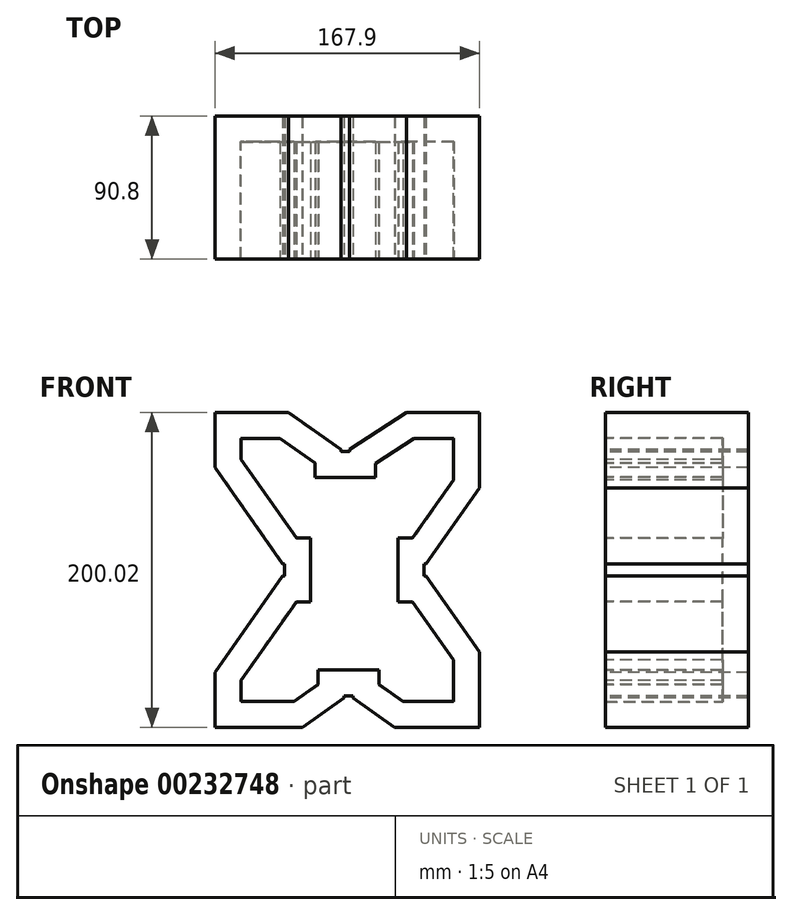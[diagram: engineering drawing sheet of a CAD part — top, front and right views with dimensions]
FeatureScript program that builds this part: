
annotation { "Feature Type Name" : "Feature", "Feature Type Description" : "" }
export const myFeature = defineFeature(function(context is Context, id is Id, definition is map)
    precondition{}
    {
        {
            var Q0;
            Q0=qCreatedBy(makeId("Front.planeOp"),FACE);
            var sketch = newSketch(context, id + "F0", { "sketchPlane" : qUnion([Q0])});
            skLineSegment(sketch, "E0.bottom", {"start": v(83.95, 100.01) * mm, "end": v(-83.95, 100.01) * mm});
            skLineSegment(sketch, "E0.top", {"start": v(83.95, -100.01) * mm, "end": v(-83.95, -100.01) * mm});
            skLineSegment(sketch, "E0.left", {"start": v(83.95, 100.01) * mm, "end": v(83.95, -100.01) * mm});
            skLineSegment(sketch, "E0.right", {"start": v(-83.95, 100.01) * mm, "end": v(-83.95, -100.01) * mm});
            skPoint(sketch, "E0.middle", {"position": v(0, 0) * mm});
            skSolve(sketch);
        }
        {
            var Q0;
            Q0 = qSketchRegion(id + "F0", true);
            extrude(context, id + "F1", {"entities" : qUnion([Q0]), "depth" : 90.8 * mm});
        }
        {
            var Q0;
            Q0=makeQuery(id+"F1.opExtrude","CAP_FACE",FACE,{"disambiguationData":[OSD([sQuery(id+"F0.wireOp",EDGE,"E0.bottom"),sQuery(id+"F0.wireOp",EDGE,"E0.top"),sQuery(id+"F0.wireOp",EDGE,"E0.left"),sQuery(id+"F0.wireOp",EDGE,"E0.right")])],"isStart":false});
            var sketch = newSketch(context, id + "F2", { "sketchPlane" : qUnion([Q0])});
            skLineSegment(sketch, "E1", {"start": v(-83.95, 100.01) * mm, "end": v(-37.47, 100.01) * mm});
            skLineSegment(sketch, "E2", {"start": v(-37.47, 100.01) * mm, "end": v(-3.94, 76.54) * mm});
            skLineSegment(sketch, "E3", {"start": v(-3.94, 76.54) * mm, "end": v(1.52, 76.54) * mm});
            skLineSegment(sketch, "E4", {"start": v(83.95, 100.01) * mm, "end": v(37.46, 100.01) * mm});
            skLineSegment(sketch, "E5", {"start": v(1.52, 76.54) * mm, "end": v(37.47, 100.01) * mm});
            skLineSegment(sketch, "E6", {"start": v(-83.95, 100.01) * mm, "end": v(-83.95, 65.09) * mm});
            skLineSegment(sketch, "E7", {"start": v(-83.95, -100.01) * mm, "end": v(-83.95, -65.09) * mm});
            skLineSegment(sketch, "E8", {"start": v(83.95, -100.01) * mm, "end": v(83.95, -51.98) * mm});
            skLineSegment(sketch, "E9", {"start": v(83.95, -100.01) * mm, "end": v(30.15, -100.01) * mm});
            skLineSegment(sketch, "E10", {"start": v(-83.95, -100.01) * mm, "end": v(-28.58, -100.01) * mm});
            skLineSegment(sketch, "E11", {"start": v(83.95, 100.01) * mm, "end": v(83.95, 51.98) * mm});
            skLineSegment(sketch, "E12", {"start": v(-83.95, 65.09) * mm, "end": v(-40.97, 3.7) * mm});
            skLineSegment(sketch, "E13", {"start": v(-40.97, -3.7) * mm, "end": v(-40.97, 3.7) * mm});
            skLineSegment(sketch, "E14", {"start": v(-83.95, -65.09) * mm, "end": v(-40.97, -3.7) * mm});
            skPoint(sketch, "E15.orphan", {"position": v(-40.97, -13.72) * mm});
            skLineSegment(sketch, "E16", {"start": v(83.95, 51.98) * mm, "end": v(50.15, 3.7) * mm});
            skLineSegment(sketch, "E17", {"start": v(83.95, -51.98) * mm, "end": v(50.15, -3.7) * mm});
            skLineSegment(sketch, "E18", {"start": v(50.15, -3.7) * mm, "end": v(50.15, 3.7) * mm});
            skLineSegment(sketch, "E19", {"start": v(-28.58, -100.01) * mm, "end": v(-1.94, -81.36) * mm});
            skLineSegment(sketch, "E20", {"start": v(-1.94, -81.36) * mm, "end": v(3.52, -81.36) * mm});
            skLineSegment(sketch, "E21", {"start": v(3.52, -81.36) * mm, "end": v(30.15, -100.01) * mm});
            skLineSegment(sketch, "E22", {"start": v(-83.95, 65.09) * mm, "end": v(-83.95, -65.09) * mm});
            skLineSegment(sketch, "E23", {"start": v(-37.47, 100.01) * mm, "end": v(37.46, 100.01) * mm});
            skLineSegment(sketch, "E24", {"start": v(83.95, 51.98) * mm, "end": v(83.95, -51.98) * mm});
            skLineSegment(sketch, "E25", {"start": v(30.15, -100.01) * mm, "end": v(-28.58, -100.01) * mm});
            skLineSegment(sketch, "E26", {"start": v(-3.94, 76.54) * mm, "end": v(-3.94, 75.27) * mm});
            skLineSegment(sketch, "E27", {"start": v(1.52, 75.27) * mm, "end": v(-3.94, 75.27) * mm});
            skLineSegment(sketch, "E28", {"start": v(1.52, 76.54) * mm, "end": v(1.52, 75.27) * mm});
            skLineSegment(sketch, "E29", {"start": v(50.15, 3.7) * mm, "end": v(48.88, 3.7) * mm});
            skLineSegment(sketch, "E30", {"start": v(48.88, -3.7) * mm, "end": v(48.88, 3.7) * mm});
            skLineSegment(sketch, "E31", {"start": v(48.88, -3.7) * mm, "end": v(50.15, -3.7) * mm});
            skLineSegment(sketch, "E32", {"start": v(-40.97, 3.7) * mm, "end": v(-39.7, 3.7) * mm});
            skLineSegment(sketch, "E33", {"start": v(-40.97, -3.7) * mm, "end": v(-39.7, -3.7) * mm});
            skLineSegment(sketch, "E34", {"start": v(-39.7, -3.7) * mm, "end": v(-39.7, 3.7) * mm});
            skLineSegment(sketch, "E35", {"start": v(-1.94, -81.36) * mm, "end": v(-1.94, -80.1) * mm});
            skLineSegment(sketch, "E36", {"start": v(-1.94, -80.1) * mm, "end": v(3.52, -80.1) * mm});
            skLineSegment(sketch, "E37", {"start": v(3.52, -80.1) * mm, "end": v(3.52, -81.36) * mm});
            skSolve(sketch);
        }
        {
            var Q0;
            Q0=makeQuery(id+"F2.imprint","IMPRINT",FACE,{"disambiguationData":[TD([[makeQuery(id+"F2.imprint","IMPRINT",EDGE,{"derivedFrom":sQuery(id+"F2.wireOp",EDGE,"E2")}),1.0]])]});
            var Q1;
            Q1=makeQuery(id+"F2.imprint","IMPRINT",FACE,{"disambiguationData":[TD([[makeQuery(id+"F2.imprint","IMPRINT",EDGE,{"derivedFrom":sQuery(id+"F2.wireOp",EDGE,"E12")}),-1.0]])]});
            var Q2;
            Q2=makeQuery(id+"F2.imprint","IMPRINT",FACE,{"disambiguationData":[TD([[makeQuery(id+"F2.imprint","IMPRINT",EDGE,{"derivedFrom":sQuery(id+"F2.wireOp",EDGE,"E16")}),1.0]])]});
            var Q3;
            Q3=makeQuery(id+"F2.imprint","IMPRINT",FACE,{"disambiguationData":[TD([[makeQuery(id+"F2.imprint","IMPRINT",EDGE,{"derivedFrom":sQuery(id+"F2.wireOp",EDGE,"E19")}),-1.0]])]});
            var Q4;
            Q4=makeQuery(id+"F2.imprint","IMPRINT",FACE,{"disambiguationData":[TD([[makeQuery(id+"F2.imprint","IMPRINT",EDGE,{"derivedFrom":sQuery(id+"F2.wireOp",EDGE,"E13")}),-1.0]])]});
            var Q5;
            Q5=makeQuery(id+"F2.imprint","IMPRINT",FACE,{"disambiguationData":[TD([[makeQuery(id+"F2.imprint","IMPRINT",EDGE,{"derivedFrom":sQuery(id+"F2.wireOp",EDGE,"E18")}),1.0]])]});
            var Q6;
            Q6=makeQuery(id+"F2.imprint","IMPRINT",FACE,{"disambiguationData":[TD([[makeQuery(id+"F2.imprint","IMPRINT",EDGE,{"derivedFrom":sQuery(id+"F2.wireOp",EDGE,"E3")}),-1.0]])]});
            var Q7;
            Q7=makeQuery(id+"F2.imprint","IMPRINT",FACE,{"disambiguationData":[TD([[makeQuery(id+"F2.imprint","IMPRINT",EDGE,{"derivedFrom":sQuery(id+"F2.wireOp",EDGE,"E20")}),1.0]])]});
            extrude(context, id + "F3", {"entities" : qUnion([Q0, Q1, Q2, Q3, Q4, Q5, Q6, Q7]), "operationType" : NewBodyOperationType.REMOVE, "endBound" : BoundingType.THROUGH_ALL, "oppositeDirection" : true, "depth" : 25.4 * mm});
        }
        {
            var Q0;
            Q0=makeQuery(id+"F1.opExtrude","CAP_FACE",FACE,{"disambiguationData":[OSD([sQuery(id+"F0.wireOp",EDGE,"E0.bottom"),sQuery(id+"F0.wireOp",EDGE,"E0.top"),sQuery(id+"F0.wireOp",EDGE,"E0.left"),sQuery(id+"F0.wireOp",EDGE,"E0.right")])],"isStart":false});
            shell(context, id + "F4", {"entities" : qUnion([Q0]), "thickness" : 16.5 * mm});
        }
        {
            var Q0;
            Q0=makeQuery(id+"F1.opExtrude","CAP_FACE",FACE,{"disambiguationData":[OSD([sQuery(id+"F0.wireOp",EDGE,"E0.bottom"),sQuery(id+"F0.wireOp",EDGE,"E0.top"),sQuery(id+"F0.wireOp",EDGE,"E0.left"),sQuery(id+"F0.wireOp",EDGE,"E0.right")])],"isStart":true});
            shell(context, id + "F5", {"entities" : qUnion([Q0]), "thickness" : 0.25 * mm});
        }
    });
